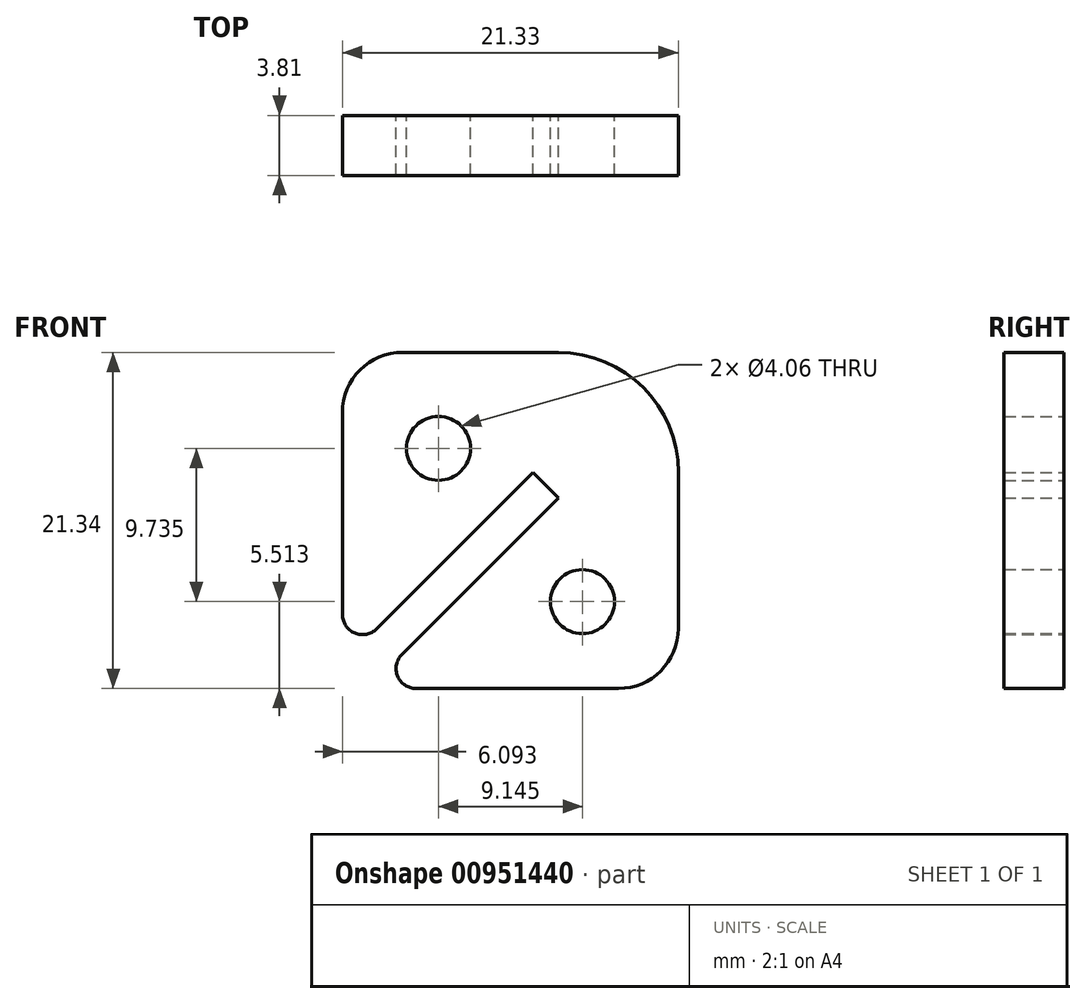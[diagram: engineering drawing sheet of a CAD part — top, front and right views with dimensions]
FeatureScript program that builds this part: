
annotation { "Feature Type Name" : "Feature", "Feature Type Description" : "" }
export const myFeature = defineFeature(function(context is Context, id is Id, definition is map)
    precondition{}
    {
        {
            var Q0;
            Q0=qCreatedBy(makeId("Front.planeOp"),FACE);
            var sketch = newSketch(context, id + "F0", { "sketchPlane" : qUnion([Q0])});
            skLineSegment(sketch, "E0", {"start": v(2.17, 2.17) * mm, "end": v(12.7, 12.7) * mm});
            skLineSegment(sketch, "E1", {"start": v(12.7, 12.7) * mm, "end": v(14.32, 11.08) * mm});
            skLineSegment(sketch, "E2", {"start": v(14.32, 11.08) * mm, "end": v(4.38, 1.14) * mm});
            skLineSegment(sketch, "E3", {"start": v(0, -3.23) * mm, "end": v(-14.32, 11.08) * mm});
            skLineSegment(sketch, "E4", {"start": v(-14.32, 11.08) * mm, "end": v(-12.7, 12.7) * mm});
            skLineSegment(sketch, "E5", {"start": v(-12.7, 12.7) * mm, "end": v(0, 0) * mm});
            skLineSegment(sketch, "E6", {"start": v(0, 3.07) * mm, "end": v(0, 6.35) * mm, "construction": true});
            skCircle(sketch, "E7", {"center": v(0, 6.35) * mm, "radius": 19.05 * mm});
            skLineSegment(sketch, "E8", {"start": v(0, 0) * mm, "end": v(0, 16.5) * mm});
            skLineSegment(sketch, "E9", {"start": v(3.81, 20.32) * mm, "end": v(14.32, 20.32) * mm});
            skLineSegment(sketch, "E10", {"start": v(21.94, 12.7) * mm, "end": v(21.94, 2.79) * mm});
            skCircle(sketch, "E11", {"center": v(6.1, 14.22) * mm, "radius": 2.29 * mm});
            skCircle(sketch, "E12", {"center": v(15.84, 4.49) * mm, "radius": 2.29 * mm});
            skLineSegment(sketch, "E13", {"start": v(18.13, -1.02) * mm, "end": v(5.28, -1.02) * mm});
            skPoint(sketch, "E14.visualSharp", {"position": v(21.94, 20.32) * mm});
            skArc(sketch, "E14.filletArc", {"start": v(21.94, 12.7) * mm, "mid": v(19.7, 18.09) * mm, "end": v(14.32, 20.32) * mm});
            skPoint(sketch, "E15.visualSharp", {"position": v(0, 20.32) * mm});
            skArc(sketch, "E15.filletArc", {"start": v(3.81, 20.32) * mm, "mid": v(1.12, 19.2) * mm, "end": v(0, 16.5) * mm});
            skPoint(sketch, "E16.visualSharp", {"position": v(21.94, -1.02) * mm});
            skArc(sketch, "E16.filletArc", {"start": v(18.13, -1.02) * mm, "mid": v(20.82, 0.1) * mm, "end": v(21.94, 2.79) * mm});
            skPoint(sketch, "E17.visualSharp", {"position": v(0, 0) * mm});
            skArc(sketch, "E17.filletArc", {"start": v(0, 3.07) * mm, "mid": v(0.78, 1.9) * mm, "end": v(2.17, 2.17) * mm});
            skPoint(sketch, "E18.newPointA", {"position": v(0, -3.23) * mm});
            skArc(sketch, "E18.filletArc", {"start": v(4.38, 1.14) * mm, "mid": v(4.1, -0.24) * mm, "end": v(5.28, -1.02) * mm});
            skSolve(sketch);
        }
        {
            var Q0;
            Q0=qCreatedBy(makeId("Front.planeOp"),FACE);
            var sketch = newSketch(context, id + "F1", { "sketchPlane" : qUnion([Q0])});
            skLineSegment(sketch, "E19", {"start": v(-4.51, -5.64) * mm, "end": v(5.42, 4.3) * mm});
            skLineSegment(sketch, "E20", {"start": v(5.42, 4.3) * mm, "end": v(7.03, 2.68) * mm});
            skLineSegment(sketch, "E21", {"start": v(7.03, 2.68) * mm, "end": v(-2.9, -7.26) * mm});
            skLineSegment(sketch, "E22", {"start": v(-2.87, 11.91) * mm, "end": v(7.03, 11.91) * mm});
            skLineSegment(sketch, "E23", {"start": v(14.65, 4.3) * mm, "end": v(14.65, -5.62) * mm});
            skCircle(sketch, "E24", {"center": v(-0.59, 5.82) * mm, "radius": 2.03 * mm});
            skCircle(sketch, "E25", {"center": v(8.56, -3.92) * mm, "radius": 2.03 * mm});
            skLineSegment(sketch, "E26", {"start": v(10.84, -9.43) * mm, "end": v(-2, -9.43) * mm});
            skPoint(sketch, "E27.visualSharp", {"position": v(14.65, 11.91) * mm});
            skArc(sketch, "E27.filletArc", {"start": v(14.65, 4.3) * mm, "mid": v(12.42, 9.68) * mm, "end": v(7.03, 11.91) * mm});
            skPoint(sketch, "E28.visualSharp", {"position": v(-6.68, 11.91) * mm});
            skArc(sketch, "E28.filletArc", {"start": v(-2.87, 11.91) * mm, "mid": v(-5.57, 10.8) * mm, "end": v(-6.68, 8.1) * mm});
            skPoint(sketch, "E29.visualSharp", {"position": v(14.65, -9.43) * mm});
            skArc(sketch, "E29.filletArc", {"start": v(10.84, -9.43) * mm, "mid": v(13.54, -8.31) * mm, "end": v(14.65, -5.62) * mm});
            skPoint(sketch, "E30.visualSharp", {"position": v(-6.68, -7.8) * mm});
            skArc(sketch, "E30.filletArc", {"start": v(-6.68, -4.74) * mm, "mid": v(-5.9, -5.91) * mm, "end": v(-4.51, -5.64) * mm});
            skArc(sketch, "E31.filletArc", {"start": v(-2.9, -7.26) * mm, "mid": v(-3.18, -8.65) * mm, "end": v(-2, -9.43) * mm});
            skLineSegment(sketch, "E32", {"start": v(-6.68, -4.74) * mm, "end": v(-6.68, 8.1) * mm});
            skSolve(sketch);
        }
        {
            var Q0;
            Q0=makeQuery(id+"F1.imprint","IMPRINT",FACE,{"disambiguationData":[TD([[makeQuery(id+"F1.imprint","IMPRINT",EDGE,{"derivedFrom":sQuery(id+"F1.wireOp",EDGE,"E19")}),1.0]])]});
            var Q1;
            Q1=makeQuery(id+"F1.imprint","IMPRINT",FACE,{"disambiguationData":[TD([[makeQuery(id+"F1.imprint","IMPRINT",EDGE,{"derivedFrom":sQuery(id+"F1.wireOp",EDGE,"E23")}),-1.0]])]});
            extrude(context, id + "F2", {"entities" : qUnion([Q0, Q1]), "depth" : 3.8 * mm, "offsetDistance" : 25.4 * mm});
        }
    });
